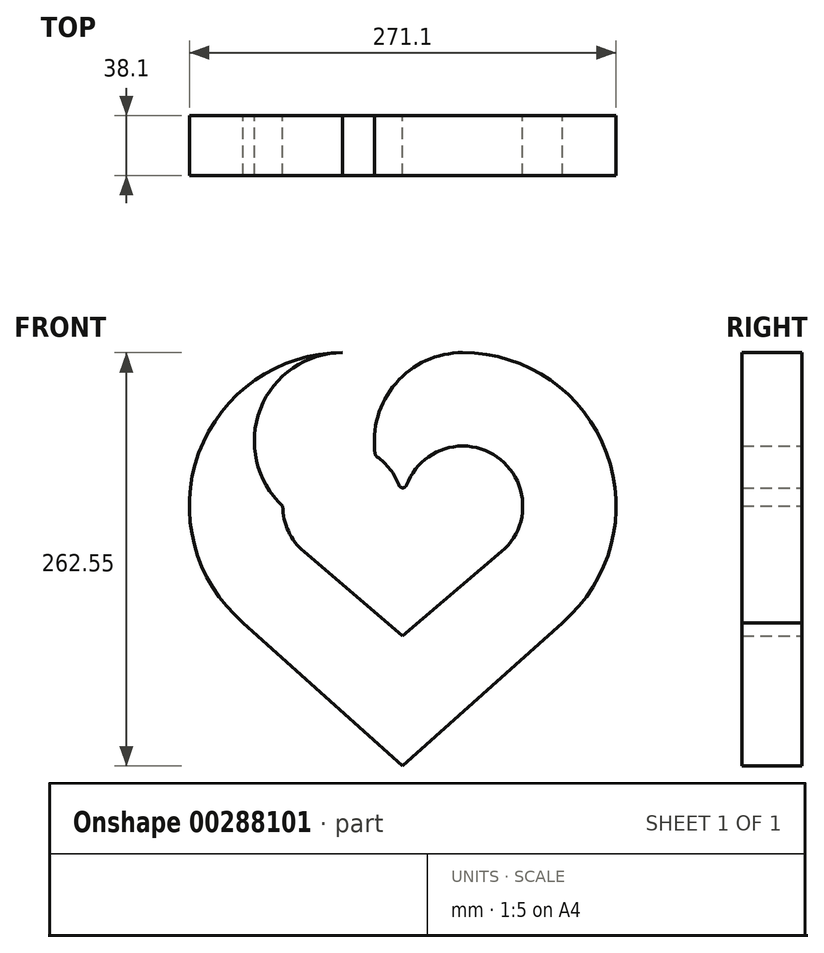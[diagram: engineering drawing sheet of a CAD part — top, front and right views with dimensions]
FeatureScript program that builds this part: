
annotation { "Feature Type Name" : "Feature", "Feature Type Description" : "" }
export const myFeature = defineFeature(function(context is Context, id is Id, definition is map)
    precondition{}
    {
        {
            var Q0;
            Q0=qCreatedBy(makeId("Front.planeOp"),FACE);
            var sketch = newSketch(context, id + "F0", { "sketchPlane" : qUnion([Q0])});
            skLineSegment(sketch, "E0", {"start": v(0, 0) * mm, "end": v(-76.2, 0) * mm});
            skLineSegment(sketch, "E1", {"start": v(0, 0) * mm, "end": v(76.2, 0) * mm});
            skLineSegment(sketch, "E2", {"start": v(0, 0) * mm, "end": v(-38.1, 0) * mm});
            skLineSegment(sketch, "E3", {"start": v(0, 0) * mm, "end": v(38.1, 0) * mm});
            skCircle(sketch, "E4", {"center": v(-38.1, 0) * mm, "radius": 38.1 * mm});
            skCircle(sketch, "E5", {"center": v(38.1, 0) * mm, "radius": 38.1 * mm});
            skLineSegment(sketch, "E6", {"start": v(-38.1, 0) * mm, "end": v(-62.82, -29) * mm});
            skLineSegment(sketch, "E7", {"start": v(38.1, 0) * mm, "end": v(62.82, -29) * mm});
            skLineSegment(sketch, "E8", {"start": v(0, 0) * mm, "end": v(0, -41.48) * mm});
            skLineSegment(sketch, "E9", {"start": v(-62.82, -29) * mm, "end": v(0, -82.55) * mm});
            skLineSegment(sketch, "E10", {"start": v(0, -82.55) * mm, "end": v(62.82, -29) * mm});
            skLineSegment(sketch, "E11", {"start": v(0, 0) * mm, "end": v(0, -82.55) * mm});
            skLineSegment(sketch, "E12", {"start": v(0, 0) * mm, "end": v(-63.5, 0) * mm});
            skLineSegment(sketch, "E13", {"start": v(0, 0) * mm, "end": v(63.5, 0) * mm});
            skLineSegment(sketch, "E14", {"start": v(-38.1, 0) * mm, "end": v(-50.8, 0) * mm});
            skLineSegment(sketch, "E15", {"start": v(38.1, 0) * mm, "end": v(50.8, 0) * mm});
            skLineSegment(sketch, "E16", {"start": v(0, 0) * mm, "end": v(0, 82.55) * mm});
            skLineSegment(sketch, "E17", {"start": v(-76.2, 0) * mm, "end": v(-38.1, 41.28) * mm});
            skLineSegment(sketch, "E18", {"start": v(-38.1, 41.28) * mm, "end": v(-76.2, 0) * mm});
            skLineSegment(sketch, "E19", {"start": v(76.2, 0) * mm, "end": v(38.1, 41.28) * mm});
            skCircle(sketch, "E20", {"center": v(-38.1, 41.28) * mm, "radius": 56.17 * mm});
            skCircle(sketch, "E21", {"center": v(38.1, 41.28) * mm, "radius": 56.17 * mm});
            skArc(sketch, "E22", {"start": v(-38.1, 97.45) * mm, "mid": v(-129.54, 33.69) * mm, "end": v(-101.32, -74.16) * mm});
            skArc(sketch, "E23", {"start": v(38.1, 97.45) * mm, "mid": v(129.54, 33.69) * mm, "end": v(101.32, -74.16) * mm});
            skLineSegment(sketch, "E24", {"start": v(0, -82.55) * mm, "end": v(0, -165.1) * mm});
            skLineSegment(sketch, "E25", {"start": v(0, -165.1) * mm, "end": v(-101.32, -74.16) * mm});
            skLineSegment(sketch, "E26", {"start": v(0, -165.1) * mm, "end": v(101.32, -74.16) * mm});
            skSolve(sketch);
        }
        {
            var Q0;
            {var subQ4=sQuery(id+"F0.wireOp",EDGE,"E9");Q0=makeQuery(id+"F0.imprint","IMPRINT",FACE,{"disambiguationData":[TD([[makeQuery(id+"F0.imprint","IMPRINT",EDGE,{"derivedFrom":subQ4}),-1.0]])]});}
            var Q1;
            {var subQ4=sQuery(id+"F0.wireOp",EDGE,"E10");Q1=makeQuery(id+"F0.imprint","IMPRINT",FACE,{"disambiguationData":[TD([[makeQuery(id+"F0.imprint","IMPRINT",EDGE,{"derivedFrom":subQ4}),-1.0]])]});}
            var Q2;
            {var subQ4=sQuery(id+"F0.wireOp",EDGE,"E5");var subQ6=sQuery(id+"F0.wireOp",EDGE,"E19");var subQ7=makeQuery(id+"F0.imprint","INTERSECT",VERTEX,{"derivedFrom":[subQ4,subQ6]});Q2=makeQuery(id+"F0.imprint","IMPRINT",FACE,{"disambiguationData":[TD([[makeQuery(id+"F0.imprint","IMPRINT",EDGE,{"disambiguationData":[TD([[subQ7,-1.0]])],"derivedFrom":subQ4}),-1.0]])]});}
            var Q3;
            {var subQ2=sQuery(id+"F0.wireOp",EDGE,"E16");Q3=makeQuery(id+"F0.imprint","IMPRINT",FACE,{"disambiguationData":[TD([[makeQuery(id+"F0.imprint","IMPRINT",EDGE,{"derivedFrom":subQ2}),1.0]])]});}
            var Q4;
            {var subQ2=sQuery(id+"F0.wireOp",EDGE,"E16");Q4=makeQuery(id+"F0.imprint","IMPRINT",FACE,{"disambiguationData":[TD([[makeQuery(id+"F0.imprint","IMPRINT",EDGE,{"derivedFrom":subQ2}),-1.0]])]});}
            var Q5;
            {var subQ1=sQuery(id+"F0.wireOp",EDGE,"E18");var subQ2=sQuery(id+"F0.wireOp",EDGE,"E4");var subQ7=makeQuery(id+"F0.imprint","INTERSECT",VERTEX,{"derivedFrom":[subQ2,subQ1]});Q5=makeQuery(id+"F0.imprint","IMPRINT",FACE,{"disambiguationData":[TD([[makeQuery(id+"F0.imprint","IMPRINT",EDGE,{"disambiguationData":[TD([[subQ7,1.0]])],"derivedFrom":subQ2}),-1.0]])]});}
            extrude(context, id + "F1", {"entities" : qUnion([Q0, Q1, Q2, Q3, Q4, Q5]), "depth" : 38.1 * mm});
        }
        {
            var Q0;
            Q0=makeQuery(id+"F1.opExtrude","SWEPT_EDGE",EDGE,{"disambiguationData":[OSD([sQuery(id+"F0.wireOp",EDGE,"E4"),sQuery(id+"F0.wireOp",EDGE,"E5"),sQuery(id+"F0.wireOp",EDGE,"E11"),sQuery(id+"F0.wireOp",EDGE,"E12"),sQuery(id+"F0.wireOp",EDGE,"E13"),sQuery(id+"F0.wireOp",EDGE,"E16"),sQuery(id+"F0.wireOp",EDGE,"E20"),sQuery(id+"F0.wireOp",EDGE,"E21")])]});
            fillet(context, id + "F2", {"entities" : qUnion([Q0]), "radius" : 2.54 * mm, "tangentPropagation" : true, "allowEdgeOverflow" : false});
        }
    });
